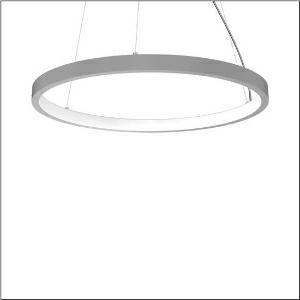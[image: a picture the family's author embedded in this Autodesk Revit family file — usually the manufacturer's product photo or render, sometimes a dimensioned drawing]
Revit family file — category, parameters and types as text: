
# Revit family: silica_r__21_ring-i_5pjbi4d1204a_fa15
name_source: partatom
category: Lighting Fixtures
units: mm (PartAtom-declared; Revit-internal decimal feet)

## family parameters
Cut with Voids When Loaded = No
Host = Face
Light Source = No
Part Type = Normal
Room Calculation Point = No
Round Connector Dimension = Use Diameter
Shared = No

## types (1)
- Silica® 21 Ring-I (1 x LED, 8460 lm, 140 W, 3000K)
    Apparent Load = 140 VA
    CIE Flux Codes = 22 48 76 50 101
    Color Rendering = 80
    Color Temperature = 3000K
    Default Elevation = 1800 mm
    Description = Silica® 21 Ring-I, suspended luminaire, of PMMA, frosted, light emission: inner ring side luminous distribution, primary light characteristic: symmetric, installation type: suspended mounting, LED, rated luminous flux: 8.460lm, luminous efficacy: 61lm/W, light colour: 830, colour temperature: 3000K, control gear: DALI 2, with terminal, 5-pole, mains connection: 230V, AC/DC, 0/50..60Hz, rated input power: 140W, housing, of extruded aluminium section, metallic grey (RAL 9006), diameter: 1.470mm, ceiling canopy, metallic grey (RAL 9006), protection rating (lamp compartment): IP40, insulation class (complete): insulation class I (protective earthing), certification: CE, impact resistance: IK02, permissible operating ambient temperature: 0..+35°C, packaging unit: 1 piece
    Height = 48 mm  [stored 0.15748 ft]
    Lamp = 1 x LED
    Lamp Light Flux = 8460 lm
    Lamp Power = 140 W
    Lamp count = 1
    Length = 1470 mm
    Luminous efficacy = 60 lm/W
    Manufacturer = Siteco
    ModVariant = No
    Model = 5PJBI4D1204A
    Mounting Place = Ceiling
    Mounting Type = Pendant
    Number of Poles = 1
    OnlyDefault = Yes
    Power Factor = 1
    Product Name = Silica® 21 Ring-I
    Product group = suspended luminaire
    ProductGroupID = 905
    Protection Class = Protection class I
    Protection Degree = IP 40
    RLX_Detail_Level = 1
    RLX_Emergency_Light_Flux = 0 lm
    RLX_Emergency_Type = 0
    RLX_Emergency_Type_DB = No
    RlxData = <blob elided: 18861 chars, md5=197dba89>
    Socket = socket
    Standby Power = 0 W
    System Light Flux = 8460 lm
    System Power = 140 W
    Type Comments = Product without accessories
    Type Image = l_1251756.jpg
    URL = http://relux.com
    VarID = ---
    Voltage = 0 V
    Weight = 0.00 kg
    Width = 0 mm  [stored 0 ft]

note: [stored X ft] marks values corroborated as IEEE doubles in the binary element streams (Revit-internal decimal feet)

## geometry (parser evidence)
native form markers: Blend x4, Sweep x12
no freeform markers — native parametric forms only
